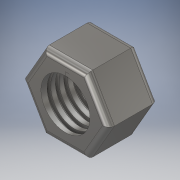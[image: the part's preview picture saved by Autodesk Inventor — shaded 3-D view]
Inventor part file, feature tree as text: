
AUTODESK INVENTOR PART (.ipt)
format: ipt  version: 2019 (Build 230136000, 136)  size: 329,216 bytes
history: native  units: mm
features: sketch x3, extrude x2, fillet x1, helix x1
ambient origin geometry x8: Origin, YZ Plane, XZ Plane, XY Plane, X Axis, Y Axis, Z Axis, Center Point
bodies: Solid1 (feature_tree)
feature tree (7):
  extrude  "Extrusion1"  Depth=5.369358mm
  extrude  "Extrusion2"  Depth=7.0mm
  fillet  "Fillet1"  Radius=7.0mm
  helix  "Coil1"  [1 undecoded]
  sketch  "Sketch1"  dims[d0=12.4mm d1=5.369358mm]
  sketch  "Sketch2"  dims[d2=7.0mm d3=0.0mm d4=7.0mm d5=7.0mm d6=0.0mm d7=0.8mm]
  sketch  "Sketch3"  dims[d8=0.5mm d9=0.5mm d10=10.0mm d11=7.0mm d12=58.9mm d13=0.0mm d14=90.0deg d15=90.0deg d16=0.0mm d17=0.0mm]
note: 1 required parameter value undecoded (feature->parameter linkage not recoverable at this tier; creation-order binding heuristic only, values carry confidence <= 0.55)
